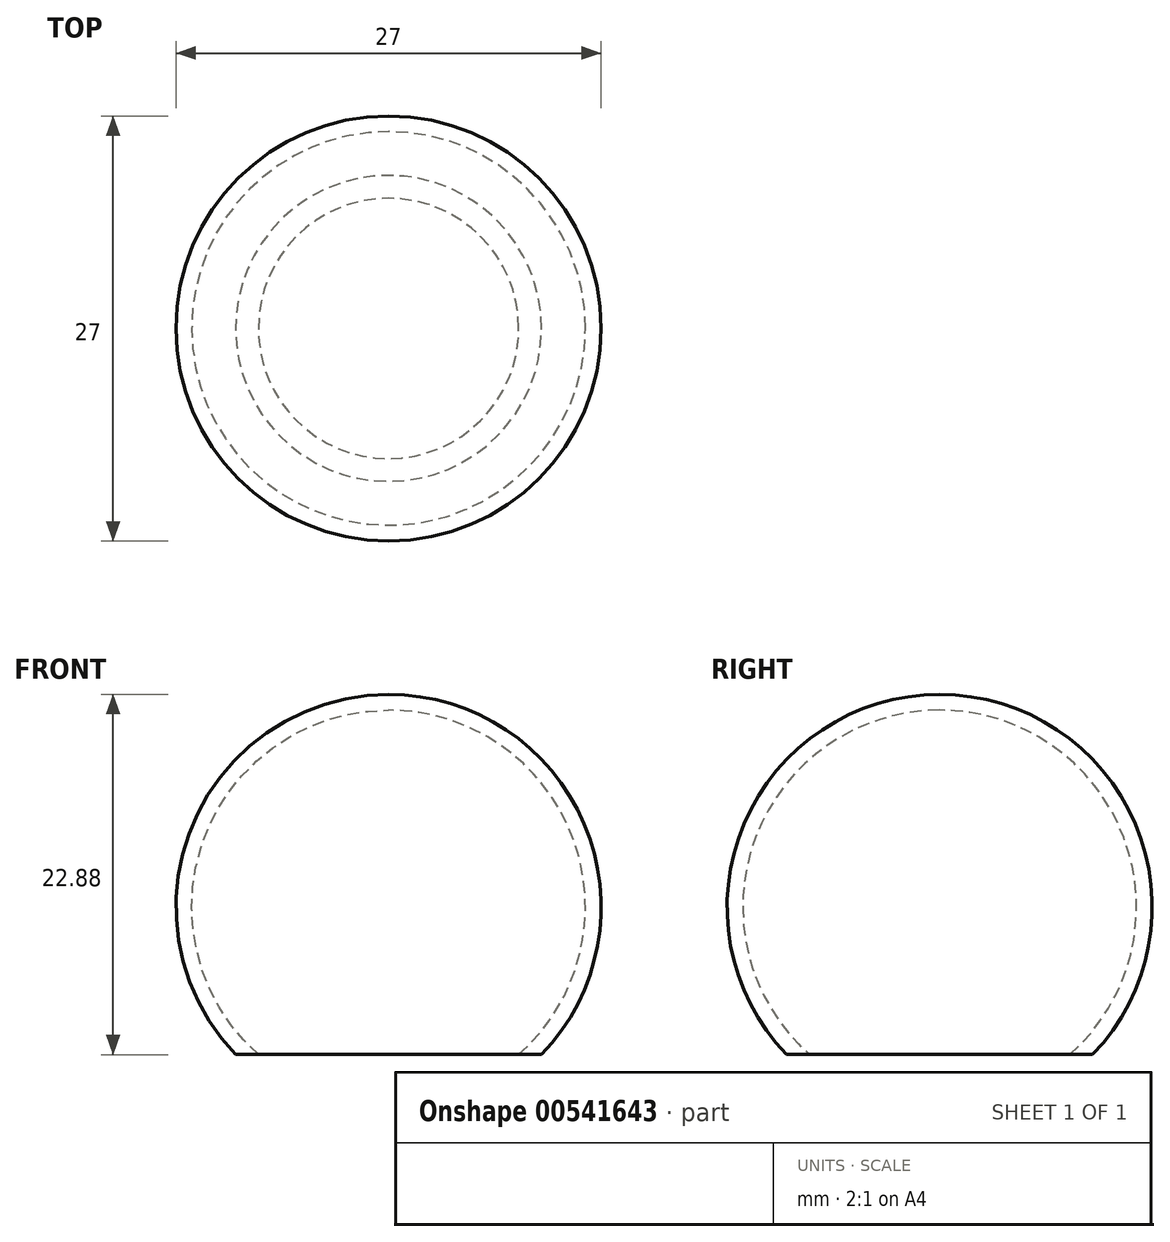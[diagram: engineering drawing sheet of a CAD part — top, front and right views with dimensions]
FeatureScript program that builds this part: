
annotation { "Feature Type Name" : "Feature", "Feature Type Description" : "" }
export const myFeature = defineFeature(function(context is Context, id is Id, definition is map)
    precondition{}
    {
        {
            var Q0;
            Q0=qCreatedBy(makeId("Front.planeOp"),FACE);
            var sketch = newSketch(context, id + "F0", { "sketchPlane" : qUnion([Q0])});
            skCircle(sketch, "E0", {"center": v(0, 0) * mm, "radius": 13.5 * mm});
            skLineSegment(sketch, "E1", {"start": v(0, 13.5) * mm, "end": v(0, -13.5) * mm});
            skSolve(sketch);
        }
        {
            var Q0;
            {var subQ0=sQuery(id+"F0.wireOp",EDGE,"E1");Q0=makeQuery(id+"F0.imprint","IMPRINT",FACE,{"disambiguationData":[TD([[makeQuery(id+"F0.imprint","IMPRINT",EDGE,{"derivedFrom":subQ0}),1.0]])]});}
            var Q1;
            Q1=sQuery(id+"F0.wireOp",EDGE,"E1");
            revolve(context, id + "F1", {"entities" : qUnion([Q0]), "axis" : qUnion([Q1]), "revolveType" : RevolveType.FULL});
        }
        {
            var Q0;
            Q0=qCreatedBy(makeId("Front.planeOp"),FACE);
            var sketch = newSketch(context, id + "F2", { "sketchPlane" : qUnion([Q0])});
            skLineSegment(sketch, "E2.bottom", {"start": v(-19.86, 24.4) * mm, "end": v(21.18, 24.4) * mm});
            skLineSegment(sketch, "E2.top", {"start": v(-19.86, -21.72) * mm, "end": v(21.18, -21.72) * mm});
            skLineSegment(sketch, "E2.left", {"start": v(-19.86, 24.4) * mm, "end": v(-19.86, -21.72) * mm});
            skLineSegment(sketch, "E2.right", {"start": v(21.18, 24.4) * mm, "end": v(21.18, -21.72) * mm});
            skLineSegment(sketch, "E3", {"start": v(-19.86, -9.38) * mm, "end": v(21.18, -9.38) * mm});
            skSolve(sketch);
        }
        {
            var Q0;
            {var subQ0=sQuery(id+"F2.wireOp",EDGE,"E2.top");Q0=makeQuery(id+"F2.imprint","IMPRINT",FACE,{"disambiguationData":[TD([[makeQuery(id+"F2.imprint","IMPRINT",EDGE,{"derivedFrom":subQ0}),1.0]])]});}
            extrude(context, id + "F3", {"entities" : qUnion([Q0]), "operationType" : NewBodyOperationType.REMOVE, "endBound" : BoundingType.SYMMETRIC, "oppositeDirection" : true, "depth" : 50.8 * mm, "offsetDistance" : 25.4 * mm});
        }
        {
            var Q0;
            Q0=makeQuery(id+"F3.boolean.opBoolean","COPY",FACE,{"derivedFrom":makeQuery(id+"F3.opExtrude","SWEPT_FACE",FACE,{"disambiguationData":[OSD([sQuery(id+"F2.wireOp",EDGE,"E3")])]})});
            shell(context, id + "F4", {"entities" : qUnion([Q0]), "thickness" : 1 * mm});
        }
    });
